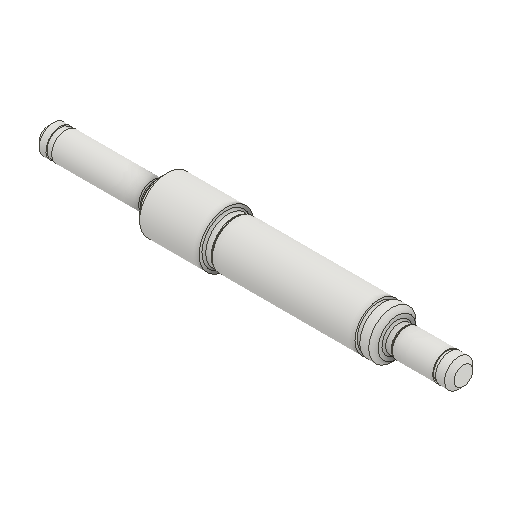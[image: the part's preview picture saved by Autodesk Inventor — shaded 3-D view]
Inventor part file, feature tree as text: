
AUTODESK INVENTOR PART (.ipt)
format: ipt  version: 2025.1 (Build 291241000, 241)  size: 202,752 bytes
history: native  units: mm
features: other x17, chamfer x4, revolve x1
ambient origin geometry x6: Origin, XZ Plane, XY Plane, X Axis, Y Axis, Z Axis
bodies: Body1 (feature_tree)
feature tree (22):
  other  "{BB8FE430-83BF-418D-8DF9-9B323D3DB9B9}"
  other  "Bryła1"
  revolve  "Obrót1"
  chamfer  "Faza5"  [1 undecoded]
  chamfer  "Faza1"  Distance=3.0mm
  other  "Podcięcie1"
  other  "Rowek dla pierścienia zabezpieczającego1"
  other  "Podcięcie2"
  chamfer  "Faza3"  Distance=5.8mm
  other  "Rowek dla pierścienia zabezpieczającego2"
  other  "Podcięcie3"
  chamfer  "Faza4"  Distance=5.0mm
  other  "Rowek dla pierścienia zabezpieczającego3"
  other  "Płaszczyzna początkowa"
  other  "Punkt początkowy"
  other  "Szkic główny"
  other  "iFeature2:1"
  other  "iFeature27:1"
  other  "iFeature2:2"
  other  "iFeature27:2"
  other  "iFeature2:3"
  other  "iFeature27:3"
note: 1 required parameter value undecoded (feature->parameter linkage not recoverable at this tier; creation-order binding heuristic only, values carry confidence <= 0.55)
